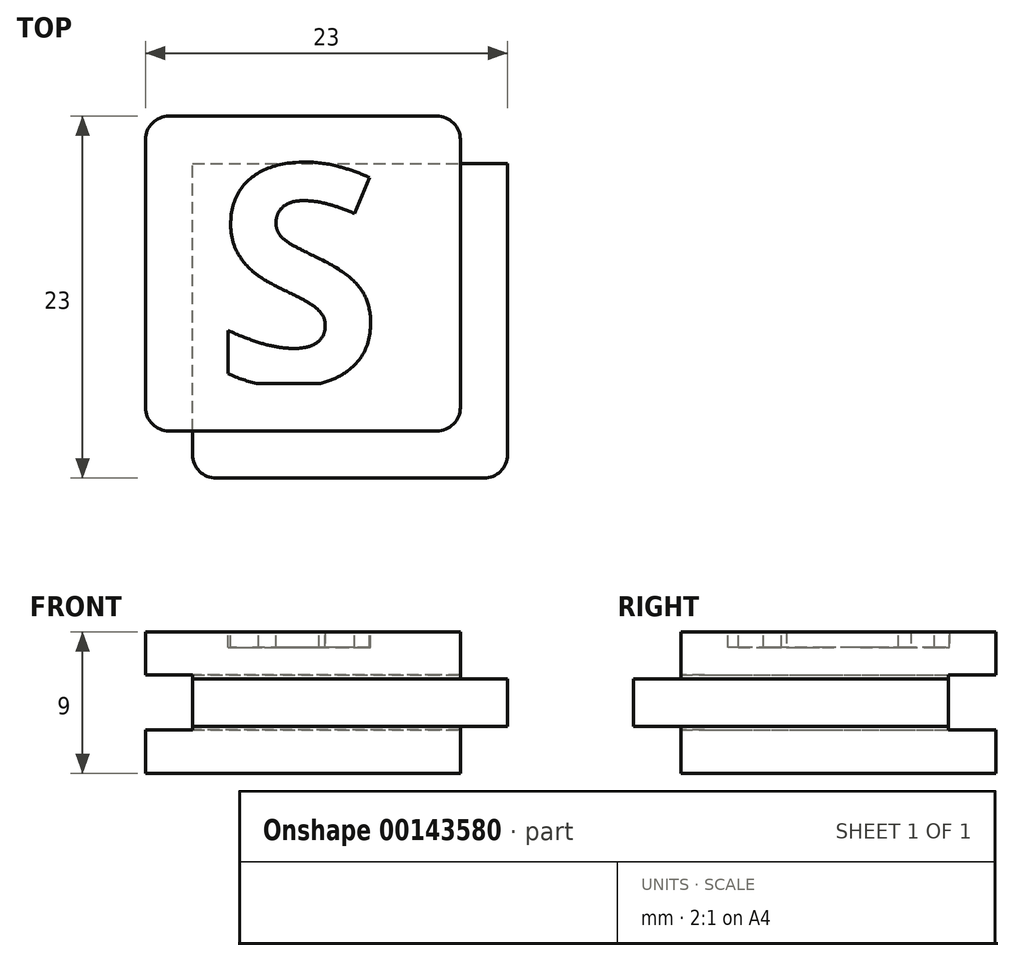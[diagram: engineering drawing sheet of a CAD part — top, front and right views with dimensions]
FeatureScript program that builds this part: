
annotation { "Feature Type Name" : "Feature", "Feature Type Description" : "" }
export const myFeature = defineFeature(function(context is Context, id is Id, definition is map)
    precondition{}
    {
        {
            var Q0;
            Q0=qCreatedBy(makeId("Front.planeOp"),FACE);
            var sketch = newSketch(context, id + "F0", { "sketchPlane" : qUnion([Q0])});
            skLineSegment(sketch, "E0.bottom", {"start": v(10, 4.5) * mm, "end": v(-10, 4.5) * mm});
            skLineSegment(sketch, "E0.top", {"start": v(10, -4.5) * mm, "end": v(-10, -4.5) * mm});
            skLineSegment(sketch, "E0.left", {"start": v(10, 4.5) * mm, "end": v(10, -4.5) * mm});
            skLineSegment(sketch, "E0.right", {"start": v(-10, 4.5) * mm, "end": v(-10, -4.5) * mm});
            skPoint(sketch, "E0.middle", {"position": v(0, 0) * mm});
            skLineSegment(sketch, "E1.bottom", {"start": v(13, 1.5) * mm, "end": v(7, 1.5) * mm});
            skLineSegment(sketch, "E1.top", {"start": v(13, -1.5) * mm, "end": v(7, -1.5) * mm});
            skLineSegment(sketch, "E1.left", {"start": v(13, 1.5) * mm, "end": v(13, -1.5) * mm});
            skLineSegment(sketch, "E1.right", {"start": v(7, 1.5) * mm, "end": v(7, -1.5) * mm});
            skPoint(sketch, "E1.middle", {"position": v(10, 0) * mm});
            skLineSegment(sketch, "E2.bottom", {"start": v(7, 1.5) * mm, "end": v(-7, 1.5) * mm});
            skLineSegment(sketch, "E2.top", {"start": v(7, -1.5) * mm, "end": v(-7, -1.5) * mm});
            skLineSegment(sketch, "E2.right", {"start": v(-7, 1.5) * mm, "end": v(-7, -1.5) * mm});
            skLineSegment(sketch, "E3.bottom", {"start": v(-7, -1.5) * mm, "end": v(-10, -1.5) * mm});
            skLineSegment(sketch, "E3.top", {"start": v(-7, 1.5) * mm, "end": v(-10, 1.5) * mm});
            skLineSegment(sketch, "E3.left", {"start": v(-7, -1.5) * mm, "end": v(-7, 1.5) * mm});
            skLineSegment(sketch, "E3.right", {"start": v(-10, -1.5) * mm, "end": v(-10, 1.5) * mm});
            skSolve(sketch);
        }
        {
            var Q0;
            {var subQ5=sQuery(id+"F0.wireOp",EDGE,"E0.bottom");Q0=makeQuery(id+"F0.imprint","IMPRINT",FACE,{"disambiguationData":[TD([[makeQuery(id+"F0.imprint","IMPRINT",EDGE,{"derivedFrom":subQ5}),1.0]])]});}
            var Q1;
            Q1=makeQuery(id+"F0.imprint","IMPRINT",FACE,{"disambiguationData":[TD([[makeQuery(id+"F0.imprint","IMPRINT",EDGE,{"derivedFrom":sQuery(id+"F0.wireOp",EDGE,"E2.bottom")}),1.0]])]});
            var Q2;
            {var subQ5=sQuery(id+"F0.wireOp",EDGE,"E1.left");Q2=makeQuery(id+"F0.imprint","IMPRINT",FACE,{"disambiguationData":[TD([[makeQuery(id+"F0.imprint","IMPRINT",EDGE,{"derivedFrom":subQ5}),-1.0]])]});}
            var Q3;
            {var subQ5=sQuery(id+"F0.wireOp",EDGE,"E1.right");Q3=makeQuery(id+"F0.imprint","IMPRINT",FACE,{"disambiguationData":[TD([[makeQuery(id+"F0.imprint","IMPRINT",EDGE,{"derivedFrom":subQ5}),1.0]])]});}
            var Q4;
            Q4=makeQuery(id+"F0.imprint","IMPRINT",FACE,{"disambiguationData":[TD([[makeQuery(id+"F0.imprint","IMPRINT",EDGE,{"derivedFrom":sQuery(id+"F0.wireOp",EDGE,"E3.bottom")}),-1.0]])]});
            var Q5;
            {var subQ5=sQuery(id+"F0.wireOp",EDGE,"E0.top");Q5=makeQuery(id+"F0.imprint","IMPRINT",FACE,{"disambiguationData":[TD([[makeQuery(id+"F0.imprint","IMPRINT",EDGE,{"derivedFrom":subQ5}),-1.0]])]});}
            extrude(context, id + "F1", {"entities" : qUnion([Q0, Q1, Q2, Q3, Q4, Q5]), "oppositeDirection" : true, "depth" : 20 * mm});
        }
        {
            var Q0;
            Q0=makeQuery(id+"F0.imprint","IMPRINT",FACE,{"disambiguationData":[TD([[makeQuery(id+"F0.imprint","IMPRINT",EDGE,{"derivedFrom":sQuery(id+"F0.wireOp",EDGE,"E3.bottom")}),-1.0]])]});
            var Q1;
            Q1=makeQuery(id+"F0.imprint","IMPRINT",FACE,{"disambiguationData":[TD([[makeQuery(id+"F0.imprint","IMPRINT",EDGE,{"derivedFrom":sQuery(id+"F0.wireOp",EDGE,"E2.bottom")}),1.0]])]});
            var Q2;
            {var subQ5=sQuery(id+"F0.wireOp",EDGE,"E1.right");Q2=makeQuery(id+"F0.imprint","IMPRINT",FACE,{"disambiguationData":[TD([[makeQuery(id+"F0.imprint","IMPRINT",EDGE,{"derivedFrom":subQ5}),1.0]])]});}
            var Q3;
            {var subQ5=sQuery(id+"F0.wireOp",EDGE,"E1.left");Q3=makeQuery(id+"F0.imprint","IMPRINT",FACE,{"disambiguationData":[TD([[makeQuery(id+"F0.imprint","IMPRINT",EDGE,{"derivedFrom":subQ5}),-1.0]])]});}
            extrude(context, id + "F2", {"entities" : qUnion([Q0, Q1, Q2, Q3]), "operationType" : NewBodyOperationType.ADD, "depth" : 3 * mm});
        }
        {
            var Q0;
            {var subQ0=sQuery(id+"F0.wireOp",EDGE,"E1.left");Q0=makeQuery(id+"F2.boolean.opBoolean","MERGE",FACE,{"derivedFrom":[makeQuery(id+"F1.opExtrude","SWEPT_FACE",FACE,{"disambiguationData":[OSD([subQ0])]}),makeQuery(id+"F2.opExtrude","SWEPT_FACE",FACE,{"disambiguationData":[OSD([subQ0])]})]});}
            var sketch = newSketch(context, id + "F3", { "sketchPlane" : qUnion([Q0])});
            skLineSegment(sketch, "E4.bottom", {"start": v(23, 1.75) * mm, "end": v(17, 1.75) * mm});
            skLineSegment(sketch, "E4.top", {"start": v(23, -1.75) * mm, "end": v(17, -1.75) * mm});
            skLineSegment(sketch, "E4.left", {"start": v(23, 1.75) * mm, "end": v(23, -1.75) * mm});
            skLineSegment(sketch, "E4.right", {"start": v(17, 1.75) * mm, "end": v(17, -1.75) * mm});
            skPoint(sketch, "E4.middle", {"position": v(20, 0) * mm});
            skSolve(sketch);
        }
        {
            var Q0;
            {var subQ1=sQuery(id+"F3.wireOp",EDGE,"E4.bottom");Q0=makeQuery(id+"F3.imprint","IMPRINT",FACE,{"disambiguationData":[TD([[makeQuery(id+"F3.imprint","IMPRINT",EDGE,{"derivedFrom":subQ1}),1.0]])]});}
            var Q1;
            {var subQ1=sQuery(id+"F0.wireOp",EDGE,"E1.left");var subQ8=makeQuery(id+"F1.opExtrude","CAP_EDGE",EDGE,{"disambiguationData":[OSD([subQ1])],"isStart":false});Q1=makeQuery(id+"F3.imprint","IMPRINT",FACE,{"disambiguationData":[TD([[makeQuery(id+"F3.imprint","IMPRINT",EDGE,{"derivedFrom":subQ8}),-1.0]])]});}
            extrude(context, id + "F4", {"entities" : qUnion([Q0, Q1]), "operationType" : NewBodyOperationType.REMOVE, "oppositeDirection" : true, "depth" : 100 * mm});
        }
        {
            var Q0;
            Q0=makeQuery(id+"F4.boolean.opBoolean","COPY",FACE,{"derivedFrom":makeQuery(id+"F4.opExtrude","SWEPT_FACE",FACE,{"disambiguationData":[OSD([sQuery(id+"F3.wireOp",EDGE,"E4.right")])]})});
            var sketch = newSketch(context, id + "F5", { "sketchPlane" : qUnion([Q0])});
            skLineSegment(sketch, "E5.bottom", {"start": v(13, 1.75) * mm, "end": v(7, 1.75) * mm});
            skLineSegment(sketch, "E5.top", {"start": v(13, -1.75) * mm, "end": v(7, -1.75) * mm});
            skLineSegment(sketch, "E5.left", {"start": v(13, 1.75) * mm, "end": v(13, -1.75) * mm});
            skLineSegment(sketch, "E5.right", {"start": v(7, 1.75) * mm, "end": v(7, -1.75) * mm});
            skPoint(sketch, "E5.middle", {"position": v(10, 0) * mm});
            skSolve(sketch);
        }
        {
            var Q0;
            {var subQ3=sQuery(id+"F5.wireOp",EDGE,"E5.left");Q0=makeQuery(id+"F5.imprint","IMPRINT",FACE,{"disambiguationData":[TD([[makeQuery(id+"F5.imprint","IMPRINT",EDGE,{"derivedFrom":subQ3}),-1.0]])]});}
            var Q1;
            {var subQ4=sQuery(id+"F5.wireOp",EDGE,"E5.right");Q1=makeQuery(id+"F5.imprint","IMPRINT",FACE,{"disambiguationData":[TD([[makeQuery(id+"F5.imprint","IMPRINT",EDGE,{"derivedFrom":subQ4}),1.0]])]});}
            extrude(context, id + "F6", {"entities" : qUnion([Q0, Q1]), "operationType" : NewBodyOperationType.REMOVE, "oppositeDirection" : true, "depth" : 100 * mm});
        }
        {
            var Q0;
            Q0=makeQuery(id+"F6.boolean.opBoolean","INTERSECT",EDGE,{"derivedFrom":[makeQuery(id+"F2.opExtrude","CAP_FACE",FACE,{"disambiguationData":[OSD([sQuery(id+"F0.wireOp",EDGE,"E1.bottom"),sQuery(id+"F0.wireOp",EDGE,"E1.top"),sQuery(id+"F0.wireOp",EDGE,"E1.left"),sQuery(id+"F0.wireOp",EDGE,"E2.bottom"),sQuery(id+"F0.wireOp",EDGE,"E2.top"),sQuery(id+"F0.wireOp",EDGE,"E3.bottom"),sQuery(id+"F0.wireOp",EDGE,"E3.top"),sQuery(id+"F0.wireOp",EDGE,"E3.right")])],"isStart":false}),makeQuery(id+"F6.opExtrude","SWEPT_FACE",FACE,{"disambiguationData":[OSD([sQuery(id+"F5.wireOp",EDGE,"E5.right")])]})]});
            var Q1;
            Q1=makeQuery(id+"F2.opExtrude","CAP_EDGE",EDGE,{"disambiguationData":[OSD([sQuery(id+"F0.wireOp",EDGE,"E1.left")])],"isStart":false});
            var Q2;
            {var subQ0=sQuery(id+"F0.wireOp",EDGE,"E0.left");Q2=makeQuery(id+"F1.opExtrude","CAP_EDGE",EDGE,{"disambiguationData":[OSD([subQ0]),TDD([makeQuery(id+"F0.imprint","IMPRINT",EDGE,{"disambiguationData":[TD([[makeQuery(id+"F0.imprint","INTERSECT",VERTEX,{"derivedFrom":[sQuery(id+"F0.wireOp",EDGE,"E0.bottom"),subQ0]}),-1.0]])],"derivedFrom":subQ0})])],"isStart":true});}
            var Q3;
            {var subQ0=sQuery(id+"F0.wireOp",EDGE,"E0.left");Q3=makeQuery(id+"F1.opExtrude","CAP_EDGE",EDGE,{"disambiguationData":[OSD([subQ0]),TDD([makeQuery(id+"F0.imprint","IMPRINT",EDGE,{"disambiguationData":[TD([[makeQuery(id+"F0.imprint","INTERSECT",VERTEX,{"derivedFrom":[sQuery(id+"F0.wireOp",EDGE,"E0.top"),subQ0]}),1.0]])],"derivedFrom":subQ0})])],"isStart":true});}
            var Q4;
            {var subQ0=sQuery(id+"F0.wireOp",EDGE,"E3.right");var subQ1=sQuery(id+"F0.wireOp",EDGE,"E0.right");var subQ3=sQuery(id+"F0.wireOp",EDGE,"E0.top");Q4=makeQuery(id+"F2.boolean.opBoolean","SPLIT",EDGE,{"disambiguationData":[TD([makeQuery(id+"F1.opExtrude","SWEPT_FACE",FACE,{"disambiguationData":[OSD([subQ3])]})])],"derivedFrom":makeQuery(id+"F1.opExtrude","CAP_EDGE",EDGE,{"disambiguationData":[OSD([subQ1,subQ0])],"isStart":true})});}
            var Q5;
            {var subQ1=sQuery(id+"F0.wireOp",EDGE,"E3.right");var subQ2=sQuery(id+"F0.wireOp",EDGE,"E0.right");var subQ3=sQuery(id+"F0.wireOp",EDGE,"E0.bottom");Q5=makeQuery(id+"F2.boolean.opBoolean","SPLIT",EDGE,{"disambiguationData":[TD([makeQuery(id+"F1.opExtrude","SWEPT_FACE",FACE,{"disambiguationData":[OSD([subQ3])]})])],"derivedFrom":makeQuery(id+"F1.opExtrude","CAP_EDGE",EDGE,{"disambiguationData":[OSD([subQ2,subQ1])],"isStart":true})});}
            var Q6;
            Q6=makeQuery(id+"F6.boolean.opBoolean","COPY",EDGE,{"derivedFrom":makeQuery(id+"F6.opExtrude","CAP_EDGE",EDGE,{"disambiguationData":[OSD([sQuery(id+"F5.wireOp",EDGE,"E5.right")])],"isStart":true})});
            var Q7;
            {var subQ0=sQuery(id+"F0.wireOp",EDGE,"E3.right");var subQ1=sQuery(id+"F0.wireOp",EDGE,"E0.right");var subQ2=sQuery(id+"F0.wireOp",EDGE,"E0.bottom");Q7=makeQuery(id+"F4.boolean.opBoolean","SPLIT",EDGE,{"disambiguationData":[TD([makeQuery(id+"F1.opExtrude","SWEPT_FACE",FACE,{"disambiguationData":[OSD([subQ2])]})])],"derivedFrom":makeQuery(id+"F1.opExtrude","CAP_EDGE",EDGE,{"disambiguationData":[OSD([subQ1,subQ0])],"isStart":false})});}
            var Q8;
            {var subQ0=sQuery(id+"F0.wireOp",EDGE,"E3.right");var subQ1=sQuery(id+"F0.wireOp",EDGE,"E0.right");var subQ2=sQuery(id+"F0.wireOp",EDGE,"E0.top");Q8=makeQuery(id+"F4.boolean.opBoolean","SPLIT",EDGE,{"disambiguationData":[TD([makeQuery(id+"F1.opExtrude","SWEPT_FACE",FACE,{"disambiguationData":[OSD([subQ2])]})])],"derivedFrom":makeQuery(id+"F1.opExtrude","CAP_EDGE",EDGE,{"disambiguationData":[OSD([subQ1,subQ0])],"isStart":false})});}
            var Q9;
            Q9=makeQuery(id+"F4.boolean.opBoolean","COPY",EDGE,{"derivedFrom":makeQuery(id+"F4.opExtrude","CAP_EDGE",EDGE,{"disambiguationData":[OSD([sQuery(id+"F3.wireOp",EDGE,"E4.right")])],"isStart":true})});
            var Q10;
            {var subQ0=sQuery(id+"F0.wireOp",EDGE,"E0.left");Q10=makeQuery(id+"F1.opExtrude","CAP_EDGE",EDGE,{"disambiguationData":[OSD([subQ0]),TDD([makeQuery(id+"F0.imprint","IMPRINT",EDGE,{"disambiguationData":[TD([[makeQuery(id+"F0.imprint","INTERSECT",VERTEX,{"derivedFrom":[sQuery(id+"F0.wireOp",EDGE,"E0.bottom"),subQ0]}),-1.0]])],"derivedFrom":subQ0})])],"isStart":false});}
            var Q11;
            {var subQ0=sQuery(id+"F0.wireOp",EDGE,"E0.left");Q11=makeQuery(id+"F1.opExtrude","CAP_EDGE",EDGE,{"disambiguationData":[OSD([subQ0]),TDD([makeQuery(id+"F0.imprint","IMPRINT",EDGE,{"disambiguationData":[TD([[makeQuery(id+"F0.imprint","INTERSECT",VERTEX,{"derivedFrom":[sQuery(id+"F0.wireOp",EDGE,"E0.top"),subQ0]}),1.0]])],"derivedFrom":subQ0})])],"isStart":false});}
            fillet(context, id + "F7", {"entities" : qUnion([Q0, Q1, Q2, Q3, Q4, Q5, Q6, Q7, Q8, Q9, Q10, Q11]), "radius" : 1.5 * mm, "tangentPropagation" : true, "allowEdgeOverflow" : false});
        }
        {
            var Q0;
            Q0=makeQuery(id+"F1.opExtrude","SWEPT_FACE",FACE,{"disambiguationData":[OSD([sQuery(id+"F0.wireOp",EDGE,"E0.bottom")])]});
            var sketch = newSketch(context, id + "F8", { "sketchPlane" : qUnion([Q0])});
            skText(sketch, "E6", { "text": "S", "fontName": "OpenSans-Bold.ttf"});
            skLineSegment(sketch, "E7.0", {"start": v(11, 3) * mm, "end": v(-11.07, 3) * mm});
            const initialGuessF8  = {"E6": [-0.00564, 0.003, 1, 0, 0.014]};
            skSetInitialGuess(sketch, initialGuessF8);
            skSolve(sketch);
        }
        {
            var Q0;
            Q0=makeQuery(id+"F8.imprint","IMPRINT",FACE,{"disambiguationData":[TD([[makeQuery(id+"F8.imprint","IMPRINT",EDGE,{"derivedFrom":sQuery(id+"F8.wireOp",EDGE,"E6.sketch_text.stroke-0")}),-1.0]])]});
            extrude(context, id + "F9", {"entities" : qUnion([Q0]), "operationType" : NewBodyOperationType.REMOVE, "oppositeDirection" : true, "depth" : 1 * mm});
        }
    });
